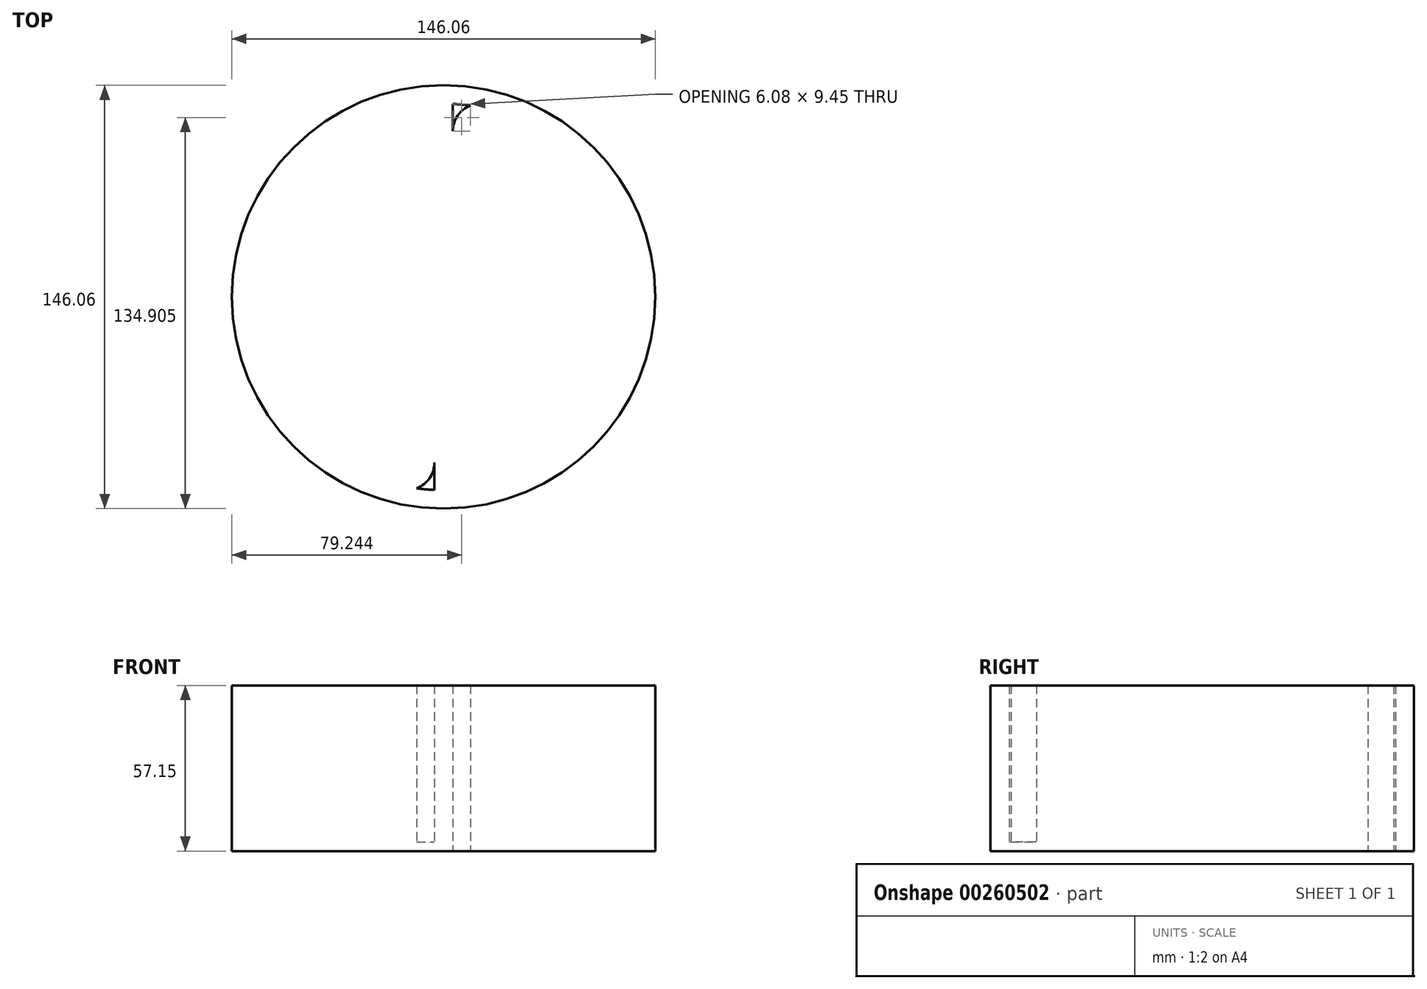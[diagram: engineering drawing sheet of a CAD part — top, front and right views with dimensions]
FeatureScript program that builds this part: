
annotation { "Feature Type Name" : "Feature", "Feature Type Description" : "" }
export const myFeature = defineFeature(function(context is Context, id is Id, definition is map)
    precondition{}
    {
        {
            var Q0;
            Q0=qCreatedBy(makeId("Top.planeOp"),FACE);
            var sketch = newSketch(context, id + "F0", { "sketchPlane" : qUnion([Q0])});
            skCircle(sketch, "E0", {"center": v(0, 0) * mm, "radius": 73.02 * mm});
            skCircle(sketch, "E1", {"center": v(0, 0) * mm, "radius": 66.68 * mm});
            skLineSegment(sketch, "E2", {"start": v(-3.18, 66.6) * mm, "end": v(-3.17, -66.6) * mm});
            skLineSegment(sketch, "E3", {"start": v(3.18, 66.6) * mm, "end": v(3.18, -66.6) * mm});
            skPoint(sketch, "E4", {"position": v(-12.7, 57.15) * mm});
            skPoint(sketch, "E5", {"position": v(12.7, 57.15) * mm});
            skPoint(sketch, "E6", {"position": v(12.7, -57.15) * mm});
            skPoint(sketch, "E7", {"position": v(-12.7, -57.15) * mm});
            skArc(sketch, "E8", {"start": v(-3.17, -57.15) * mm, "mid": v(-4.84, -62.53) * mm, "end": v(-9.25, -66.03) * mm});
            skArc(sketch, "E9", {"start": v(3.18, -57.15) * mm, "mid": v(4.84, -62.53) * mm, "end": v(9.25, -66.03) * mm});
            skArc(sketch, "E10", {"start": v(3.18, 57.15) * mm, "mid": v(4.84, 62.53) * mm, "end": v(9.25, 66.03) * mm});
            skArc(sketch, "E11", {"start": v(-3.17, 57.15) * mm, "mid": v(-4.84, 62.53) * mm, "end": v(-9.25, 66.03) * mm});
            skPoint(sketch, "E12", {"position": v(0, 73.02) * mm});
            skPoint(sketch, "E13", {"position": v(0, 66.68) * mm});
            skPoint(sketch, "E14", {"position": v(0, -66.68) * mm});
            skLineSegment(sketch, "E15", {"start": v(0, 73.02) * mm, "end": v(0, -73.02) * mm});
            skSolve(sketch);
        }
        {
            var Q0;
            Q0 = qSketchRegion(id + "F0", true);
            var Q1;
            {var subQ3=sQuery(id+"F0.wireOp",EDGE,"E11");Q1=makeQuery(id+"F0.imprint","IMPRINT",FACE,{"disambiguationData":[TD([[makeQuery(id+"F0.imprint","IMPRINT",EDGE,{"derivedFrom":subQ3}),-1.0]])]});}
            var Q2;
            {var subQ4=sQuery(id+"F0.wireOp",EDGE,"QZf0gXTj-Lq7C-IXG0-T0AA-tdFKAwPVhZjn");Q2=makeQuery(id+"F0.imprint","IMPRINT",FACE,{"disambiguationData":[TD([[makeQuery(id+"F0.imprint","IMPRINT",EDGE,{"derivedFrom":subQ4}),-1.0]])]});}
            var Q3;
            {var subQ4=sQuery(id+"F0.wireOp",EDGE,"QZf0gXTj-Lq7C-IXG0-T0AA-tdFKAwPVhZjn");Q3=makeQuery(id+"F0.imprint","IMPRINT",FACE,{"disambiguationData":[TD([[makeQuery(id+"F0.imprint","IMPRINT",EDGE,{"derivedFrom":subQ4}),1.0]])]});}
            var Q4;
            {var subQ3=sQuery(id+"F0.wireOp",EDGE,"E10");Q4=makeQuery(id+"F0.imprint","IMPRINT",FACE,{"disambiguationData":[TD([[makeQuery(id+"F0.imprint","IMPRINT",EDGE,{"derivedFrom":subQ3}),1.0]])]});}
            var Q5;
            {var subQ3=sQuery(id+"F0.wireOp",EDGE,"E9");Q5=makeQuery(id+"F0.imprint","IMPRINT",FACE,{"disambiguationData":[TD([[makeQuery(id+"F0.imprint","IMPRINT",EDGE,{"derivedFrom":subQ3}),-1.0]])]});}
            var Q6;
            {var subQ3=sQuery(id+"F0.wireOp",EDGE,"E8");Q6=makeQuery(id+"F0.imprint","IMPRINT",FACE,{"disambiguationData":[TD([[makeQuery(id+"F0.imprint","IMPRINT",EDGE,{"derivedFrom":subQ3}),1.0]])]});}
            var Q7;
            {var subQ0=sQuery(id+"F0.wireOp",EDGE,"E2");var subQ3=sQuery(id+"F0.wireOp",EDGE,"E1");var subQ4=makeQuery(id+"F0.imprint","INTERSECT",VERTEX,{"disambiguationData":[OD(0.0)],"derivedFrom":[subQ3,subQ0]});Q7=makeQuery(id+"F0.imprint","IMPRINT",FACE,{"disambiguationData":[TD([[makeQuery(id+"F0.imprint","IMPRINT",EDGE,{"disambiguationData":[TD([[subQ4,1.0]])],"derivedFrom":subQ3}),1.0]])]});}
            var Q8;
            {var subQ0=sQuery(id+"F0.wireOp",EDGE,"E3");var subQ1=sQuery(id+"F0.wireOp",EDGE,"E1");var subQ2=makeQuery(id+"F0.imprint","INTERSECT",VERTEX,{"disambiguationData":[OD(0.0)],"derivedFrom":[subQ1,subQ0]});Q8=makeQuery(id+"F0.imprint","IMPRINT",FACE,{"disambiguationData":[TD([[makeQuery(id+"F0.imprint","IMPRINT",EDGE,{"disambiguationData":[TD([[subQ2,-1.0]])],"derivedFrom":subQ1}),1.0]])]});}
            extrude(context, id + "F1", {"entities" : qUnion([Q0, Q1, Q2, Q3, Q4, Q5, Q6, Q7, Q8]), "depth" : 57.15 * mm});
        }
        {
            var Q0;
            {var subQ0=sQuery(id+"F0.wireOp",EDGE,"E8");Q0=makeQuery(id+"F0.imprint","IMPRINT",FACE,{"disambiguationData":[TD([[makeQuery(id+"F0.imprint","IMPRINT",EDGE,{"derivedFrom":subQ0}),-1.0]])]});}
            var Q1;
            {var subQ0=sQuery(id+"F0.wireOp",EDGE,"E9");Q1=makeQuery(id+"F0.imprint","IMPRINT",FACE,{"disambiguationData":[TD([[makeQuery(id+"F0.imprint","IMPRINT",EDGE,{"derivedFrom":subQ0}),1.0]])]});}
            extrude(context, id + "F2", {"entities" : qUnion([Q0, Q1]), "operationType" : NewBodyOperationType.ADD, "depth" : 3.17 * mm});
        }
    });
